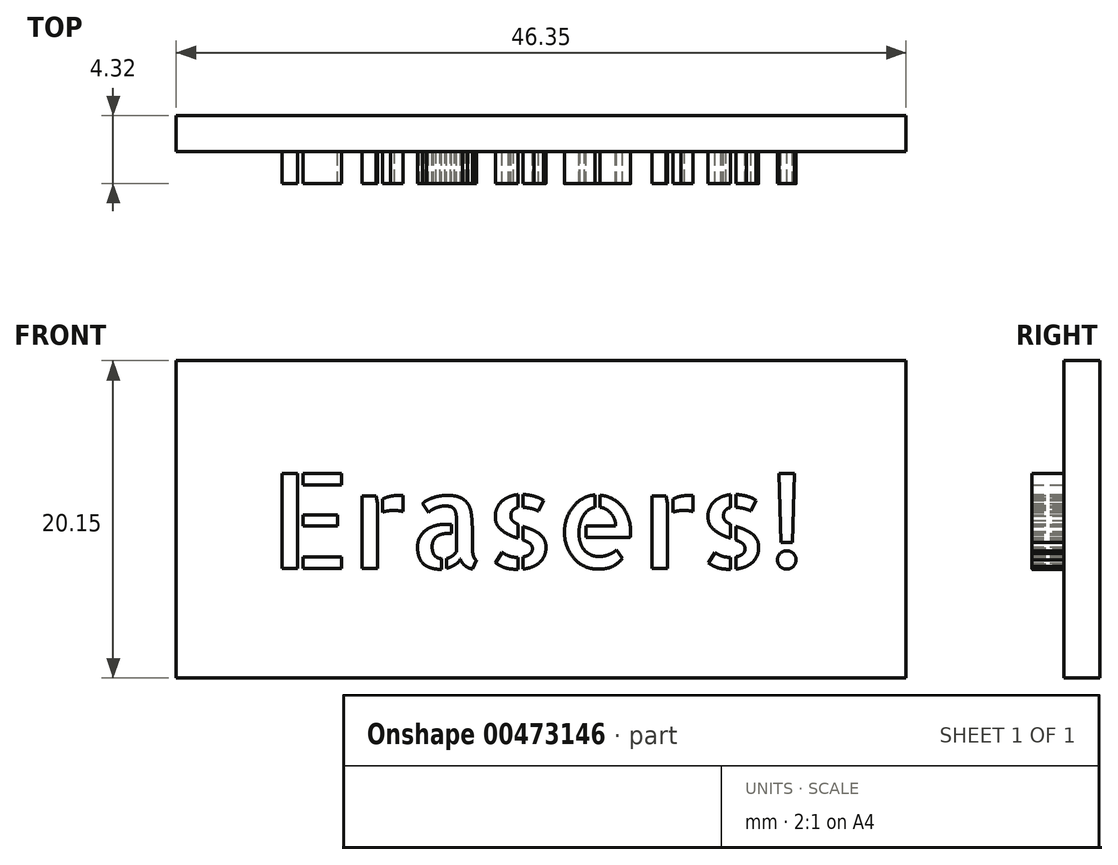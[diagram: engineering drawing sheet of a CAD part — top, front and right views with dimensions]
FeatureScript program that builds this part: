
annotation { "Feature Type Name" : "Feature", "Feature Type Description" : "" }
export const myFeature = defineFeature(function(context is Context, id is Id, definition is map)
    precondition{}
    {
        {
            var Q0;
            Q0=qCreatedBy(makeId("Front.planeOp"),FACE);
            var sketch = newSketch(context, id + "F0", { "sketchPlane" : qUnion([Q0])});
            skLineSegment(sketch, "E0.bottom", {"start": v(-48.57, 36.68) * mm, "end": v(-2.22, 36.68) * mm});
            skLineSegment(sketch, "E0.top", {"start": v(-48.57, 16.53) * mm, "end": v(-2.22, 16.53) * mm});
            skLineSegment(sketch, "E0.left", {"start": v(-48.57, 36.68) * mm, "end": v(-48.57, 16.53) * mm});
            skLineSegment(sketch, "E0.right", {"start": v(-2.22, 36.68) * mm, "end": v(-2.22, 16.53) * mm});
            skSolve(sketch);
        }
        {
            var Q0;
            Q0=makeQuery(id+"F0.imprint","IMPRINT",FACE,{"disambiguationData":[TD([[makeQuery(id+"F0.imprint","IMPRINT",EDGE,{"derivedFrom":sQuery(id+"F0.wireOp",EDGE,"E0.bottom")}),-1.0]])]});
            extrude(context, id + "F1", {"entities" : qUnion([Q0]), "depth" : 2.3 * mm});
        }
        {
            var Q0;
            Q0=qCreatedBy(makeId("Front.planeOp"),FACE);
            var sketch = newSketch(context, id + "F2", { "sketchPlane" : qUnion([Q0])});
            skText(sketch, "E1", { "text": "Erasers!", "fontName": "AllertaStencil-Regular.ttf"});
            const initialGuessF2  = {"E1": [-0.04264, 0.02347, 1, 0, 0.00605]};
            skSetInitialGuess(sketch, initialGuessF2);
            skSolve(sketch);
        }
        {
            var Q0;
            Q0 = qSketchRegion(id + "F2", true);
            extrude(context, id + "F3", {"entities" : qUnion([Q0]), "operationType" : NewBodyOperationType.ADD, "depth" : 4.32 * mm});
        }
    });
